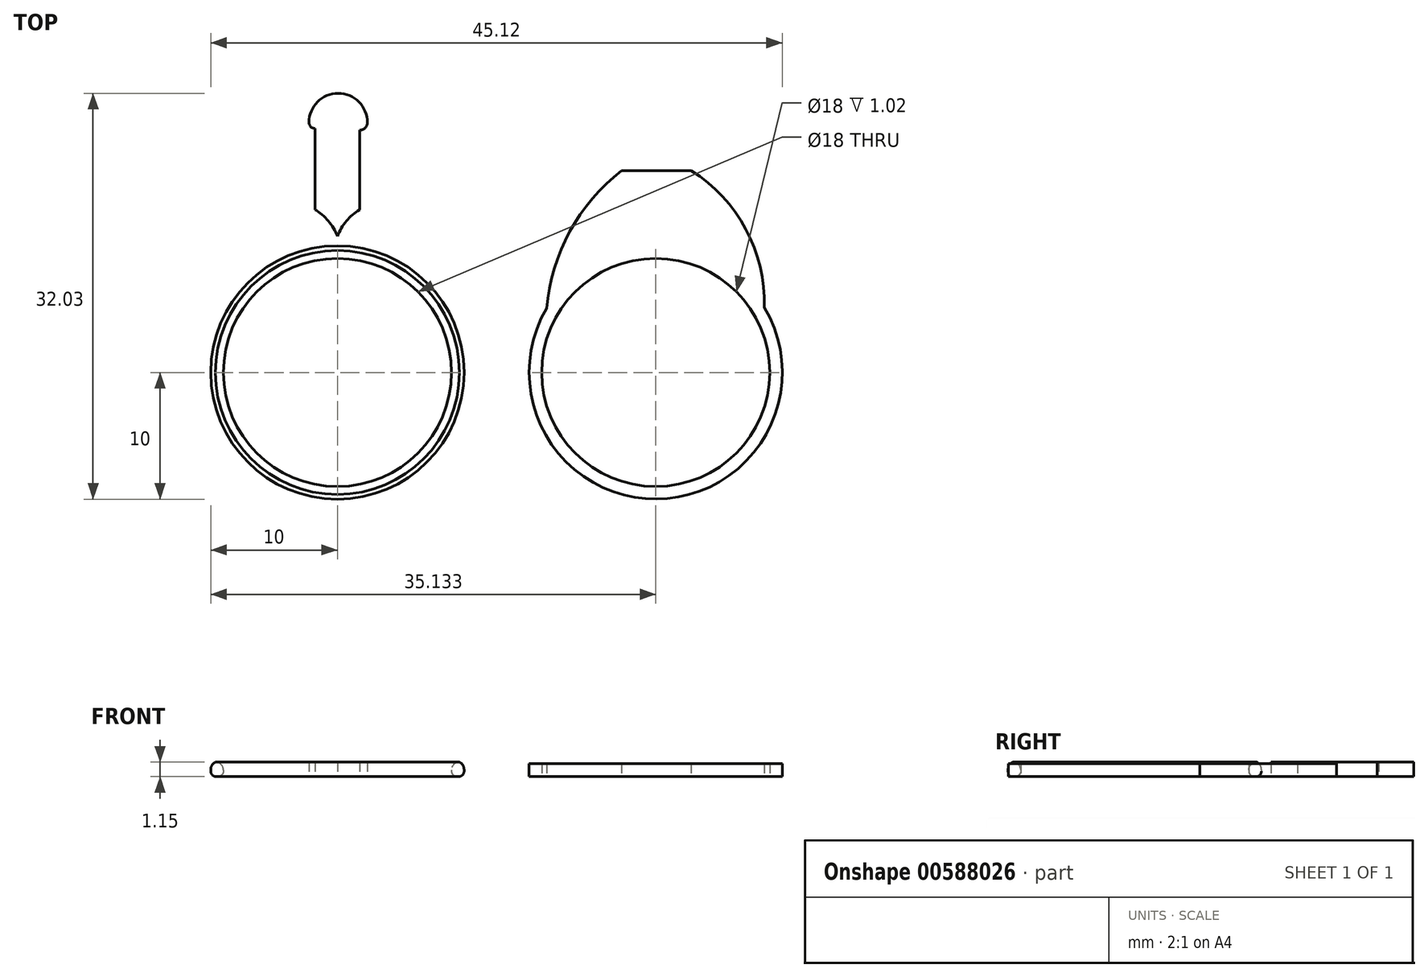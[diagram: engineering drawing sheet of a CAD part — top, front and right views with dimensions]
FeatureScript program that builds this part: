
annotation { "Feature Type Name" : "Feature", "Feature Type Description" : "" }
export const myFeature = defineFeature(function(context is Context, id is Id, definition is map)
    precondition{}
    {
        {
            var Q0;
            Q0=qCreatedBy(makeId("Top.planeOp"),FACE);
            var sketch = newSketch(context, id + "F0", { "sketchPlane" : qUnion([Q0])});
            skCircle(sketch, "E0", {"center": v(0, 0) * mm, "radius": 9 * mm});
            skCircle(sketch, "E1", {"center": v(0, 0) * mm, "radius": 10 * mm});
            skLineSegment(sketch, "E2", {"start": v(1.76, 19.12) * mm, "end": v(1.76, 12.85) * mm});
            skLineSegment(sketch, "E3.MirrorCS", {"start": v(-1.77, 19.26) * mm, "end": v(-1.78, 12.86) * mm});
            skArc(sketch, "E4.trimOffspring", {"start": v(0, 10.77) * mm, "mid": v(6.13, 12.95) * mm, "end": v(7.53, 6.59) * mm});
            skArc(sketch, "E5.trimOffspring", {"start": v(0, 10.77) * mm, "mid": v(-6.13, 12.95) * mm, "end": v(-7.53, 6.59) * mm});
            skArc(sketch, "E6.trimOffspring", {"start": v(1.76, 12.85) * mm, "mid": v(7.22, 12.09) * mm, "end": v(7.53, 6.59) * mm});
            skArc(sketch, "E7.trimOffspring", {"start": v(-1.78, 12.86) * mm, "mid": v(-7.23, 12.08) * mm, "end": v(-7.53, 6.59) * mm});
            skArc(sketch, "E8", {"start": v(2.37, 19.73) * mm, "mid": v(0.07, 22.03) * mm, "end": v(-2.24, 19.73) * mm});
            skArc(sketch, "E9", {"start": v(-2.24, 19.73) * mm, "mid": v(-2.1, 19.4) * mm, "end": v(-1.77, 19.26) * mm});
            skArc(sketch, "E10", {"start": v(1.76, 19.12) * mm, "mid": v(2.19, 19.3) * mm, "end": v(2.37, 19.73) * mm});
            skSolve(sketch);
        }
        {
            var Q0;
            Q0=makeQuery(id+"F0.imprint","IMPRINT",FACE,{"disambiguationData":[TD([[makeQuery(id+"F0.imprint","IMPRINT",EDGE,{"derivedFrom":sQuery(id+"F0.wireOp",EDGE,"E0")}),-1.0]])]});
            var Q1;
            Q1=makeQuery(id+"F0.imprint","IMPRINT",FACE,{"disambiguationData":[TD([[makeQuery(id+"F0.imprint","IMPRINT",EDGE,{"derivedFrom":sQuery(id+"F0.wireOp",EDGE,"E4.trimOffspring")}),-1.0]])]});
            var Q2;
            Q2=makeQuery(id+"F0.imprint","IMPRINT",FACE,{"disambiguationData":[TD([[makeQuery(id+"F0.imprint","IMPRINT",EDGE,{"derivedFrom":sQuery(id+"F0.wireOp",EDGE,"E2")}),-1.0]])]});
            var Q3;
            Q3=makeQuery(id+"F0.imprint","IMPRINT",FACE,{"disambiguationData":[TD([[makeQuery(id+"F0.imprint","IMPRINT",EDGE,{"derivedFrom":sQuery(id+"F0.wireOp",EDGE,"88adb5ea-b903-4bd5-9c3a-304b3481c5fb")}),-1.0]])]});
            var Q4;
            Q4=makeQuery(id+"F0.imprint","IMPRINT",FACE,{"disambiguationData":[TD([[makeQuery(id+"F0.imprint","IMPRINT",EDGE,{"derivedFrom":sQuery(id+"F0.wireOp",EDGE,"buvwp8Ql-HdYJ-HOlQ-nnd6-sbBf7QhQNz0a")}),-1.0]])]});
            extrude(context, id + "F1", {"entities" : qUnion([Q0, Q1, Q2, Q3, Q4]), "depth" : 1.15 * mm, "offsetDistance" : 25 * mm});
        }
        {
            var Q0;
            Q0=makeQuery(id+"F1.opExtrude","CAP_EDGE",EDGE,{"disambiguationData":[OSD([sQuery(id+"F0.wireOp",EDGE,"E0")])],"isStart":false});
            fillet(context, id + "F2", {"entities" : qUnion([Q0]), "radius" : 0.63 * mm, "tangentPropagation" : true, "allowEdgeOverflow" : false});
        }
        {
            var Q0;
            Q0=makeQuery(id+"F1.opExtrude","CAP_EDGE",EDGE,{"disambiguationData":[OSD([sQuery(id+"F0.wireOp",EDGE,"E0")])],"isStart":true});
            fillet(context, id + "F3", {"entities" : qUnion([Q0]), "radius" : 0.46 * mm, "tangentPropagation" : true, "allowEdgeOverflow" : false});
        }
        {
            var Q0;
            Q0=makeQuery(id+"F1.opExtrude","CAP_EDGE",EDGE,{"disambiguationData":[OSD([sQuery(id+"F0.wireOp",EDGE,"E1")])],"isStart":false});
            fillet(context, id + "F4", {"entities" : qUnion([Q0]), "radius" : 0.65 * mm, "tangentPropagation" : true, "allowEdgeOverflow" : false});
        }
        {
            var Q0;
            Q0=makeQuery(id+"F1.opExtrude","CAP_EDGE",EDGE,{"disambiguationData":[OSD([sQuery(id+"F0.wireOp",EDGE,"E1")])],"isStart":true});
            fillet(context, id + "F5", {"entities" : qUnion([Q0]), "radius" : 0.43 * mm, "tangentPropagation" : true, "allowEdgeOverflow" : false});
        }
        {
            var Q0;
            Q0=qCreatedBy(makeId("Top.planeOp"),FACE);
            var sketch = newSketch(context, id + "F6", { "sketchPlane" : qUnion([Q0])});
            skLineSegment(sketch, "E11", {"start": v(16.04, 0) * mm, "end": v(16.13, 0) * mm});
            skCircle(sketch, "E12", {"center": v(25.13, 0) * mm, "radius": 9 * mm});
            skArc(sketch, "E13", {"start": v(16.52, 5.06) * mm, "mid": v(25.18, -10) * mm, "end": v(33.7, 5.14) * mm});
            skLineSegment(sketch, "E14", {"start": v(22.44, 15.93) * mm, "end": v(27.93, 15.93) * mm});
            skArc(sketch, "E15", {"start": v(22.44, 15.93) * mm, "mid": v(18.34, 11.12) * mm, "end": v(16.52, 5.06) * mm});
            skLineSegment(sketch, "E16.trimOffspring", {"start": v(34.13, 0) * mm, "end": v(34.22, 0) * mm});
            skPoint(sketch, "E17.orphan", {"position": v(25.13, 15.93) * mm});
            skArc(sketch, "E18", {"start": v(33.7, 5.14) * mm, "mid": v(32.25, 11.3) * mm, "end": v(27.93, 15.93) * mm});
            skLineSegment(sketch, "E19", {"start": v(16.52, 5.06) * mm, "end": v(16.82, 3.46) * mm});
            skLineSegment(sketch, "E20", {"start": v(33.7, 5.14) * mm, "end": v(33.38, 3.6) * mm});
            skSolve(sketch);
        }
        {
            var Q0;
            Q0=makeQuery(id+"F6.imprint","IMPRINT",FACE,{"disambiguationData":[TD([[makeQuery(id+"F6.imprint","IMPRINT",EDGE,{"derivedFrom":sQuery(id+"F6.wireOp",EDGE,"E13")}),1.0]])]});
            var Q1;
            Q1=makeQuery(id+"F6.imprint","IMPRINT",FACE,{"disambiguationData":[TD([[makeQuery(id+"F6.imprint","IMPRINT",EDGE,{"derivedFrom":sQuery(id+"F6.wireOp",EDGE,"E14")}),-1.0]])]});
            extrude(context, id + "F7", {"entities" : qUnion([Q0, Q1]), "depth" : 1.02 * mm, "offsetDistance" : 25 * mm});
        }
    });
